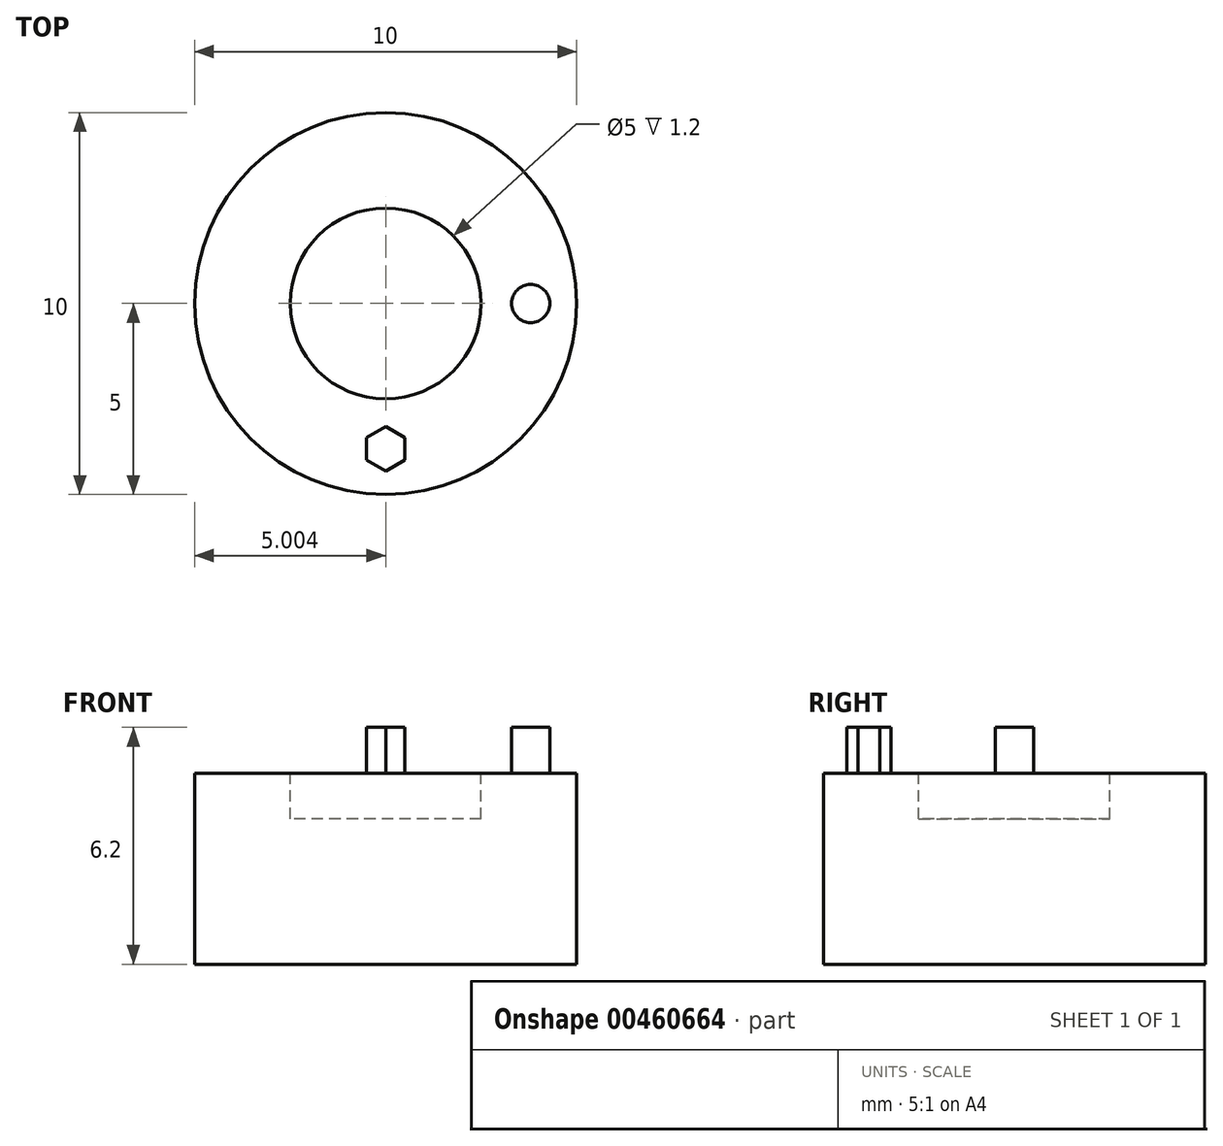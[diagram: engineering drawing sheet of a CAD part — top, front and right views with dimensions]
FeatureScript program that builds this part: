
annotation { "Feature Type Name" : "Feature", "Feature Type Description" : "" }
export const myFeature = defineFeature(function(context is Context, id is Id, definition is map)
    precondition{}
    {
        {
            var Q0;
            Q0=qCreatedBy(makeId("Top.planeOp"),FACE);
            var sketch = newSketch(context, id + "F0", { "sketchPlane" : qUnion([Q0])});
            skCircle(sketch, "E0", {"center": v(-10.54, 0) * mm, "radius": 5 * mm});
            skSolve(sketch);
        }
        {
            var Q0;
            Q0=makeQuery(id+"F0.imprint","IMPRINT",FACE,{"disambiguationData":[TD([[makeQuery(id+"F0.imprint","IMPRINT",EDGE,{"derivedFrom":sQuery(id+"F0.wireOp",EDGE,"E0")}),1.0]])]});
            extrude(context, id + "F1", {"entities" : qUnion([Q0]), "depth" : 5 * mm});
        }
        {
            var Q0;
            Q0=makeQuery(id+"F1.opExtrude","CAP_FACE",FACE,{"disambiguationData":[OSD([sQuery(id+"F0.wireOp",EDGE,"E0")])],"isStart":false});
            var sketch = newSketch(context, id + "F2", { "sketchPlane" : qUnion([Q0])});
            skCircle(sketch, "E1", {"center": v(-10.54, 0) * mm, "radius": 2.5 * mm});
            skCircle(sketch, "E2", {"center": v(-6.74, 0) * mm, "radius": 0.5 * mm});
            skCircle(sketch, "E3.cCircle", {"center": v(-10.54, -3.8) * mm, "radius": 0.5 * mm, "construction": true});
            skLineSegment(sketch, "E3.0", {"start": v(-10.03, -3.52) * mm, "end": v(-10.03, -4.1) * mm});
            skLineSegment(sketch, "E3.1", {"start": v(-10.03, -4.1) * mm, "end": v(-10.54, -4.4) * mm});
            skLineSegment(sketch, "E3.2", {"start": v(-10.54, -4.4) * mm, "end": v(-11.04, -4.1) * mm});
            skLineSegment(sketch, "E3.3", {"start": v(-11.04, -4.1) * mm, "end": v(-11.04, -3.52) * mm});
            skLineSegment(sketch, "E3.4", {"start": v(-11.04, -3.52) * mm, "end": v(-10.54, -3.23) * mm});
            skLineSegment(sketch, "E3.5", {"start": v(-10.54, -3.23) * mm, "end": v(-10.03, -3.52) * mm});
            skPoint(sketch, "E3.0.midPoint", {"position": v(-10.03, -3.8) * mm});
            skSolve(sketch);
        }
        {
            var Q0;
            Q0=makeQuery(id+"F2.imprint","IMPRINT",FACE,{"disambiguationData":[TD([[makeQuery(id+"F2.imprint","IMPRINT",EDGE,{"derivedFrom":sQuery(id+"F2.wireOp",EDGE,"E2")}),1.0]])]});
            var Q1;
            Q1=makeQuery(id+"F2.imprint","IMPRINT",FACE,{"disambiguationData":[TD([[makeQuery(id+"F2.imprint","IMPRINT",EDGE,{"derivedFrom":sQuery(id+"F2.wireOp",EDGE,"E3.0")}),-1.0]])]});
            var Q2;
            Q2=sQuery(id+"F2.wireOp",EDGE,"E1");
            extrude(context, id + "F3", {"entities" : qUnion([Q0, Q1]), "operationType" : NewBodyOperationType.ADD, "surfaceEntities" : qUnion([Q2]), "depth" : 1.2 * mm});
        }
        {
            var Q0;
            Q0=makeQuery(id+"F2.imprint","IMPRINT",FACE,{"disambiguationData":[TD([[makeQuery(id+"F2.imprint","IMPRINT",EDGE,{"derivedFrom":sQuery(id+"F2.wireOp",EDGE,"E1")}),1.0]])]});
            var Q1;
            Q1=sQuery(id+"F2.wireOp",EDGE,"E2");
            extrude(context, id + "F4", {"entities" : qUnion([Q0]), "operationType" : NewBodyOperationType.REMOVE, "surfaceEntities" : qUnion([Q1]), "oppositeDirection" : true, "depth" : 1.2 * mm});
        }
    });
